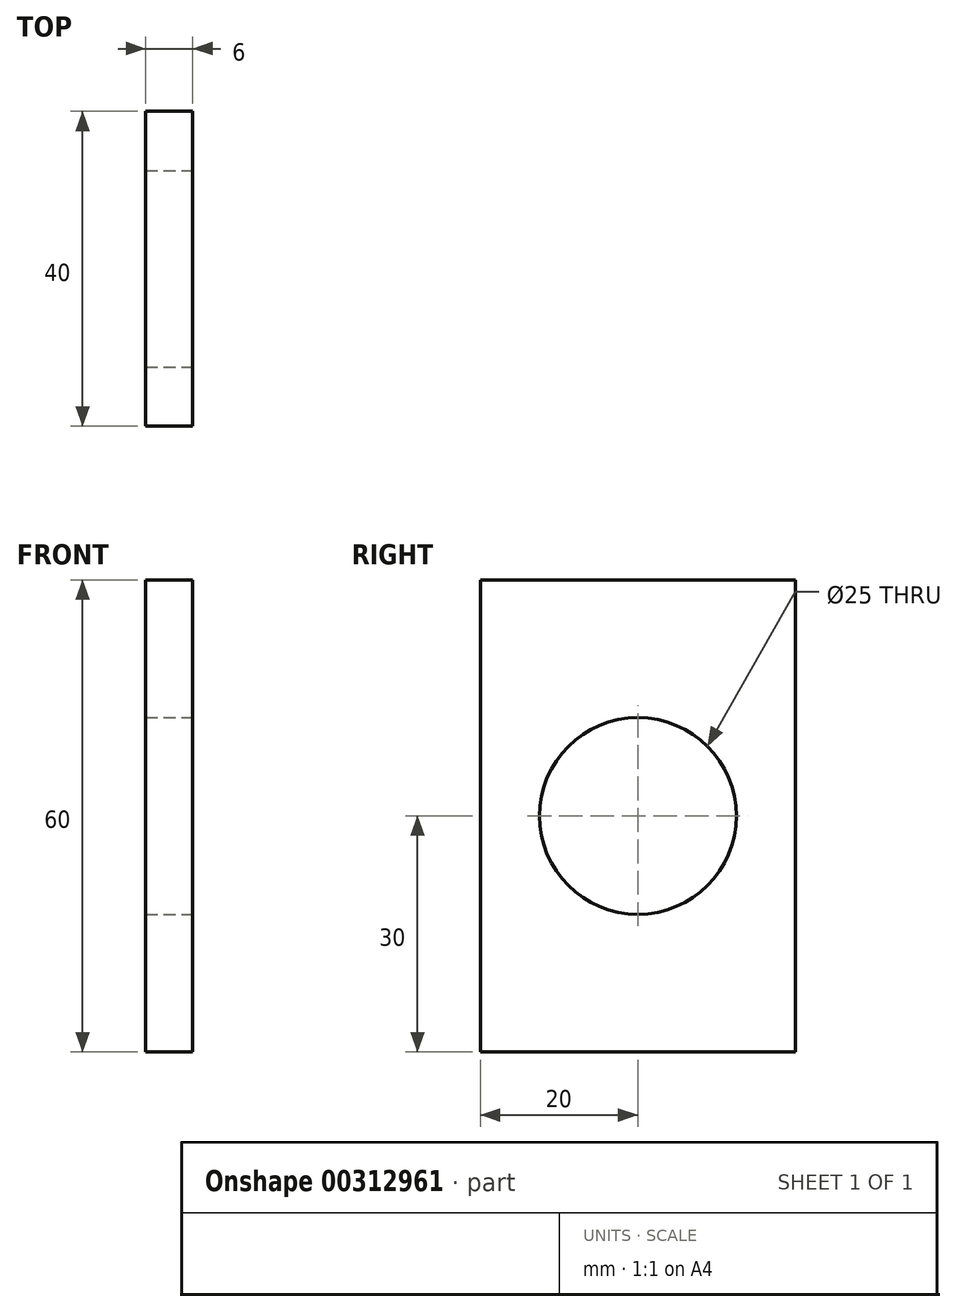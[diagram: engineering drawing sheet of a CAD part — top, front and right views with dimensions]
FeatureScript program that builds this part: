
annotation { "Feature Type Name" : "Feature", "Feature Type Description" : "" }
export const myFeature = defineFeature(function(context is Context, id is Id, definition is map)
    precondition{}
    {
        {
            var Q0;
            Q0=qCreatedBy(makeId("Right.planeOp"),FACE);
            var sketch = newSketch(context, id + "F0", { "sketchPlane" : qUnion([Q0])});
            skLineSegment(sketch, "E0.bottom", {"start": v(20, 30) * mm, "end": v(-20, 30) * mm});
            skLineSegment(sketch, "E0.top", {"start": v(20, -30) * mm, "end": v(-20, -30) * mm});
            skLineSegment(sketch, "E0.left", {"start": v(20, 30) * mm, "end": v(20, -30) * mm});
            skLineSegment(sketch, "E0.right", {"start": v(-20, 30) * mm, "end": v(-20, -30) * mm});
            skPoint(sketch, "E0.middle", {"position": v(0, 0) * mm});
            skSolve(sketch);
        }
        {
            var Q0;
            Q0=qSketchRegion(id+"F0",true);
            extrude(context, id + "F1", {"entities" : qUnion([Q0]), "depth" : 6 * mm});
        }
        {
            var Q0;
            Q0=makeQuery(id+"F1.opExtrude","CAP_FACE",FACE,{"disambiguationData":[OSD([sQuery(id+"F0.wireOp",EDGE,"E0.bottom"),sQuery(id+"F0.wireOp",EDGE,"E0.top"),sQuery(id+"F0.wireOp",EDGE,"E0.left"),sQuery(id+"F0.wireOp",EDGE,"E0.right")])],"isStart":false});
            var sketch = newSketch(context, id + "F2", { "sketchPlane" : qUnion([Q0])});
            skCircle(sketch, "E1", {"center": v(0, 0) * mm, "radius": 12.5 * mm});
            skSolve(sketch);
        }
        {
            var Q0;
            Q0=qSketchRegion(id+"F2",true);
            extrude(context, id + "F3", {"entities" : qUnion([Q0]), "operationType" : NewBodyOperationType.REMOVE, "oppositeDirection" : true, "depth" : 25 * mm});
        }
    });
